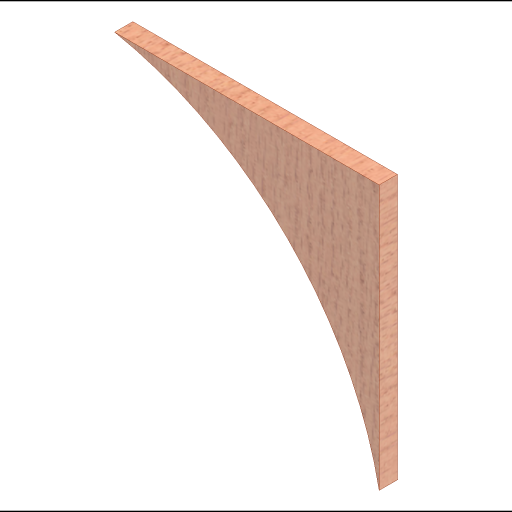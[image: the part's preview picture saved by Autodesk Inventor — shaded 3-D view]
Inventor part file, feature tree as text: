
AUTODESK INVENTOR PART (.ipt)
format: ipt  version: 2023 (Build 270158000, 158)  size: 172,544 bytes
history: native  units: in
note: dims shown in document units (in); Inventor stores cm internally (conversion verified against a paired STEP export)
features: extrude x2, sketch x2
ambient origin geometry x8: Origin, YZ Plane, XZ Plane, XY Plane, X Axis, Y Axis, Z Axis, Center Point
bodies: Solid1 (feature_tree)
feature tree (4):
  extrude  "Extrusion1"  Depth=17.0in
  extrude  "Extrusion2"  Depth=8.5in
  sketch  "Sketch1"  dims[d0=17.0in d1=17.0in]
  sketch  "Sketch2"  dims[d2=17.0in d3=8.5in d4=8.5in d5=0.47in d6=0.0in d7=17.3228in d8=0.0in d9=0.0in]
